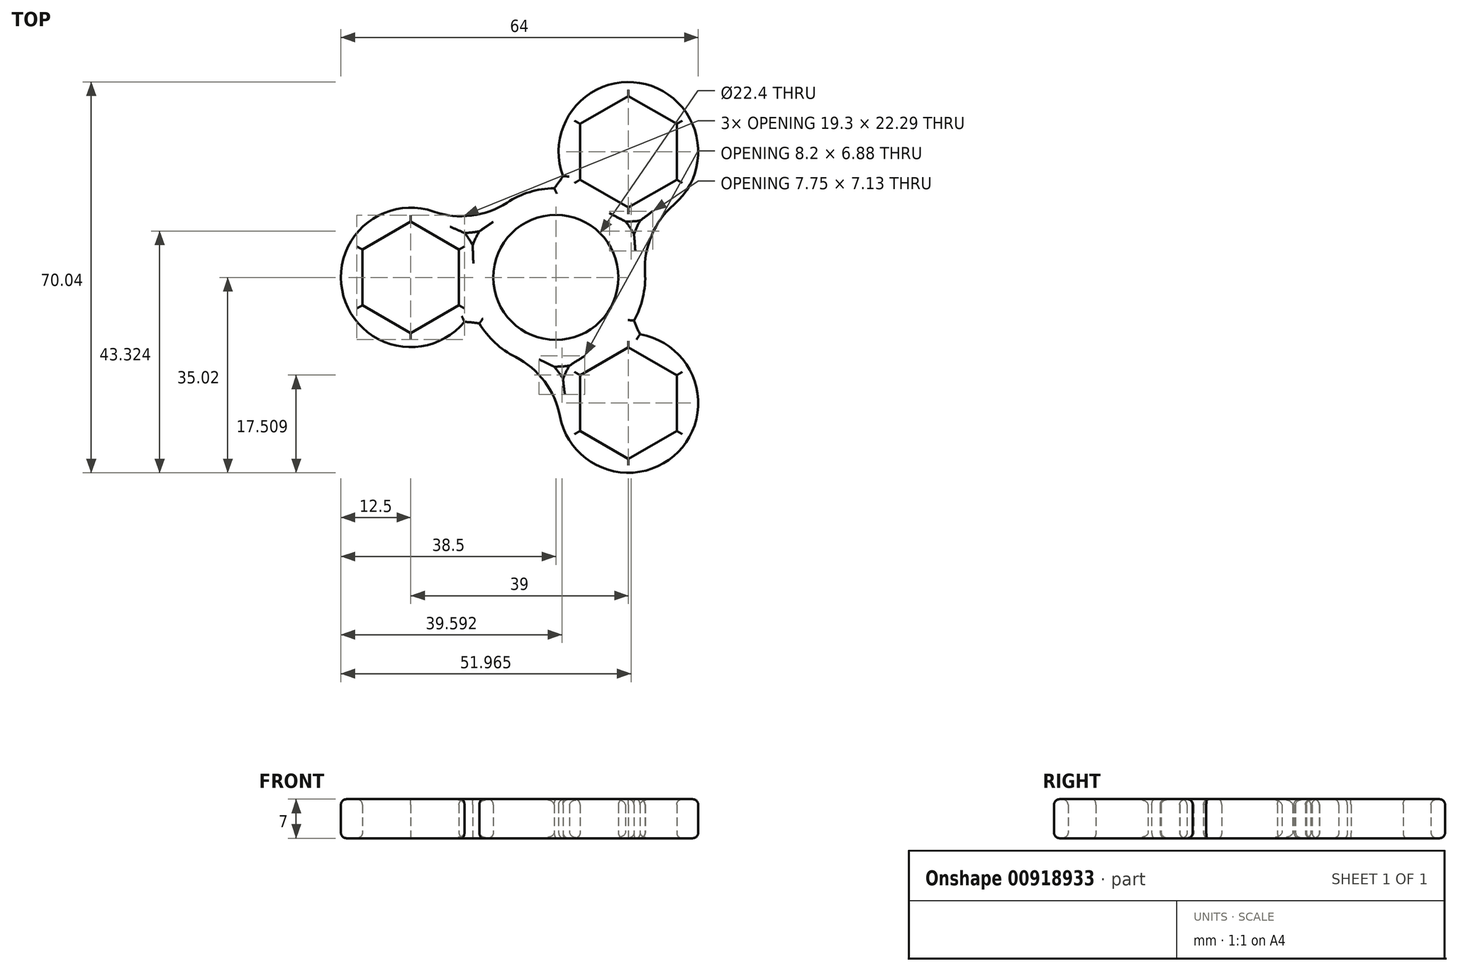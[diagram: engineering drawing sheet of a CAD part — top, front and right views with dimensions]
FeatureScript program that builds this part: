
annotation { "Feature Type Name" : "Feature", "Feature Type Description" : "" }
export const myFeature = defineFeature(function(context is Context, id is Id, definition is map)
    precondition{}
    {
        {
            var Q0;
            Q0=qCreatedBy(makeId("Top.planeOp"),FACE);
            var sketch = newSketch(context, id + "F0", { "sketchPlane" : qUnion([Q0])});
            skCircle(sketch, "E0", {"center": v(0, 0) * mm, "radius": 11.2 * mm});
            skCircle(sketch, "E1", {"center": v(0, 0) * mm, "radius": 16 * mm});
            skLineSegment(sketch, "E2", {"start": v(0, 0) * mm, "end": v(-26, 0) * mm, "construction": true});
            skCircle(sketch, "E3", {"center": v(-26, 0) * mm, "radius": 12.5 * mm});
            skArc(sketch, "E4", {"start": v(-21.88, 11.8) * mm, "mid": v(-15.13, 11.07) * mm, "end": v(-8.74, 13.4) * mm});
            skArc(sketch, "E5", {"start": v(-16.37, 7.97) * mm, "mid": v(-15.03, 8.06) * mm, "end": v(-13.7, 8.26) * mm});
            skArc(sketch, "E6.MirrorCS", {"start": v(-16.37, -7.97) * mm, "mid": v(-15.03, -8.06) * mm, "end": v(-13.7, -8.26) * mm});
            skArc(sketch, "E7.MirrorCS", {"start": v(-21.88, -11.8) * mm, "mid": v(-15.13, -11.07) * mm, "end": v(-8.74, -13.4) * mm});
            skLineSegment(sketch, "E8.1.0", {"start": v(0, 0) * mm, "end": v(13, -22.52) * mm, "construction": true});
            skCircle(sketch, "E8.1.1", {"center": v(13, -22.52) * mm, "radius": 12.5 * mm});
            skArc(sketch, "E8.1.2", {"start": v(0.72, -24.85) * mm, "mid": v(-2.03, -18.64) * mm, "end": v(-7.23, -14.27) * mm});
            skArc(sketch, "E8.1.3", {"start": v(1.28, -18.17) * mm, "mid": v(0.53, -17.05) * mm, "end": v(-0.3, -16) * mm});
            skArc(sketch, "E8.1.4", {"start": v(15.1, -10.2) * mm, "mid": v(14.5, -8.99) * mm, "end": v(14, -7.74) * mm});
            skArc(sketch, "E8.1.5", {"start": v(21.16, -13.05) * mm, "mid": v(17.15, -7.56) * mm, "end": v(15.98, -0.87) * mm});
            skLineSegment(sketch, "E8.2.0", {"start": v(0, 0) * mm, "end": v(13, 22.52) * mm, "construction": true});
            skCircle(sketch, "E8.2.1", {"center": v(13, 22.52) * mm, "radius": 12.5 * mm});
            skArc(sketch, "E8.2.2", {"start": v(21.16, 13.05) * mm, "mid": v(17.15, 7.56) * mm, "end": v(15.98, 0.87) * mm});
            skArc(sketch, "E8.2.3", {"start": v(15.1, 10.2) * mm, "mid": v(14.5, 8.99) * mm, "end": v(14, 7.74) * mm});
            skArc(sketch, "E8.2.4", {"start": v(1.28, 18.17) * mm, "mid": v(0.53, 17.05) * mm, "end": v(-0.3, 16) * mm});
            skArc(sketch, "E8.2.5", {"start": v(0.72, 24.85) * mm, "mid": v(-2.03, 18.64) * mm, "end": v(-7.23, 14.27) * mm});
            skCircle(sketch, "E9.cCircle", {"center": v(-26, 0) * mm, "radius": 8.65 * mm, "construction": true});
            skLineSegment(sketch, "E9.0", {"start": v(-17.35, 5) * mm, "end": v(-17.35, -5) * mm});
            skLineSegment(sketch, "E9.1", {"start": v(-17.35, -5) * mm, "end": v(-26, -9.99) * mm});
            skLineSegment(sketch, "E9.2", {"start": v(-26, -9.99) * mm, "end": v(-34.65, -5) * mm});
            skLineSegment(sketch, "E9.3", {"start": v(-34.65, -5) * mm, "end": v(-34.65, 5) * mm});
            skLineSegment(sketch, "E9.4", {"start": v(-34.65, 5) * mm, "end": v(-26, 9.99) * mm});
            skLineSegment(sketch, "E9.5", {"start": v(-26, 9.99) * mm, "end": v(-17.35, 5) * mm});
            skPoint(sketch, "E9.0.midPoint", {"position": v(-17.35, 0) * mm});
            skLineSegment(sketch, "E10.1.1", {"start": v(13, -32.5) * mm, "end": v(4.35, -27.51) * mm});
            skLineSegment(sketch, "E10.1.2", {"start": v(4.35, -27.51) * mm, "end": v(4.35, -17.52) * mm});
            skLineSegment(sketch, "E10.1.3", {"start": v(4.35, -17.52) * mm, "end": v(13, -12.53) * mm});
            skLineSegment(sketch, "E10.1.4", {"start": v(13, -12.53) * mm, "end": v(21.65, -17.52) * mm});
            skLineSegment(sketch, "E10.1.5", {"start": v(21.65, -17.52) * mm, "end": v(21.65, -27.51) * mm});
            skLineSegment(sketch, "E10.1.6", {"start": v(21.65, -27.51) * mm, "end": v(13, -32.5) * mm});
            skLineSegment(sketch, "E10.2.1", {"start": v(21.65, 27.51) * mm, "end": v(21.65, 17.52) * mm});
            skLineSegment(sketch, "E10.2.2", {"start": v(21.65, 17.52) * mm, "end": v(13, 12.53) * mm});
            skLineSegment(sketch, "E10.2.3", {"start": v(13, 12.53) * mm, "end": v(4.35, 17.52) * mm});
            skLineSegment(sketch, "E10.2.4", {"start": v(4.35, 17.52) * mm, "end": v(4.35, 27.51) * mm});
            skLineSegment(sketch, "E10.2.5", {"start": v(4.35, 27.51) * mm, "end": v(13, 32.5) * mm});
            skLineSegment(sketch, "E10.2.6", {"start": v(13, 32.5) * mm, "end": v(21.65, 27.51) * mm});
            skSolve(sketch);
        }
        {
            var Q0;
            {var subQ0=sQuery(id+"F0.wireOp",EDGE,"E3");var subQ4=sQuery(id+"F0.wireOp",EDGE,"E1");var subQ5=makeQuery(id+"F0.imprint","INTERSECT",VERTEX,{"disambiguationData":[OD(0.0)],"derivedFrom":[subQ4,subQ0]});Q0=makeQuery(id+"F0.imprint","IMPRINT",FACE,{"disambiguationData":[TD([[makeQuery(id+"F0.imprint","IMPRINT",EDGE,{"disambiguationData":[TD([[subQ5,-1.0]])],"derivedFrom":subQ4}),-1.0]])]});}
            var Q1;
            {var subQ0=sQuery(id+"F0.wireOp",EDGE,"E3");var subQ1=sQuery(id+"F0.wireOp",EDGE,"E1");var subQ2=makeQuery(id+"F0.imprint","INTERSECT",VERTEX,{"disambiguationData":[OD(0.0)],"derivedFrom":[subQ1,subQ0]});Q1=makeQuery(id+"F0.imprint","IMPRINT",FACE,{"disambiguationData":[TD([[makeQuery(id+"F0.imprint","IMPRINT",EDGE,{"disambiguationData":[TD([[subQ2,-1.0]])],"derivedFrom":subQ1}),1.0]])]});}
            var Q2;
            Q2=makeQuery(id+"F0.imprint","IMPRINT",FACE,{"disambiguationData":[TD([[makeQuery(id+"F0.imprint","IMPRINT",EDGE,{"derivedFrom":sQuery(id+"F0.wireOp",EDGE,"E0")}),-1.0]])]});
            var Q3;
            {var subQ0=sQuery(id+"F0.wireOp",EDGE,"E4");Q3=makeQuery(id+"F0.imprint","IMPRINT",FACE,{"disambiguationData":[TD([[makeQuery(id+"F0.imprint","IMPRINT",EDGE,{"derivedFrom":subQ0}),-1.0]])]});}
            var Q4;
            {var subQ0=sQuery(id+"F0.wireOp",EDGE,"E8.2.4");Q4=makeQuery(id+"F0.imprint","IMPRINT",FACE,{"disambiguationData":[TD([[makeQuery(id+"F0.imprint","IMPRINT",EDGE,{"derivedFrom":subQ0}),-1.0]])]});}
            var Q5;
            {var subQ0=sQuery(id+"F0.wireOp",EDGE,"E8.2.1");var subQ4=sQuery(id+"F0.wireOp",EDGE,"E1");var subQ5=makeQuery(id+"F0.imprint","INTERSECT",VERTEX,{"disambiguationData":[OD(0.0)],"derivedFrom":[subQ4,subQ0]});Q5=makeQuery(id+"F0.imprint","IMPRINT",FACE,{"disambiguationData":[TD([[makeQuery(id+"F0.imprint","IMPRINT",EDGE,{"disambiguationData":[TD([[subQ5,-1.0]])],"derivedFrom":subQ4}),-1.0]])]});}
            var Q6;
            {var subQ0=sQuery(id+"F0.wireOp",EDGE,"E8.2.1");var subQ1=sQuery(id+"F0.wireOp",EDGE,"E1");var subQ2=makeQuery(id+"F0.imprint","INTERSECT",VERTEX,{"disambiguationData":[OD(0.0)],"derivedFrom":[subQ1,subQ0]});Q6=makeQuery(id+"F0.imprint","IMPRINT",FACE,{"disambiguationData":[TD([[makeQuery(id+"F0.imprint","IMPRINT",EDGE,{"disambiguationData":[TD([[subQ2,-1.0]])],"derivedFrom":subQ1}),1.0]])]});}
            var Q7;
            {var subQ0=sQuery(id+"F0.wireOp",EDGE,"E8.2.2");Q7=makeQuery(id+"F0.imprint","IMPRINT",FACE,{"disambiguationData":[TD([[makeQuery(id+"F0.imprint","IMPRINT",EDGE,{"derivedFrom":subQ0}),-1.0]])]});}
            var Q8;
            {var subQ0=sQuery(id+"F0.wireOp",EDGE,"E8.1.4");Q8=makeQuery(id+"F0.imprint","IMPRINT",FACE,{"disambiguationData":[TD([[makeQuery(id+"F0.imprint","IMPRINT",EDGE,{"derivedFrom":subQ0}),-1.0]])]});}
            var Q9;
            {var subQ0=sQuery(id+"F0.wireOp",EDGE,"E8.1.1");var subQ4=sQuery(id+"F0.wireOp",EDGE,"E1");var subQ5=makeQuery(id+"F0.imprint","INTERSECT",VERTEX,{"disambiguationData":[OD(0.0)],"derivedFrom":[subQ4,subQ0]});Q9=makeQuery(id+"F0.imprint","IMPRINT",FACE,{"disambiguationData":[TD([[makeQuery(id+"F0.imprint","IMPRINT",EDGE,{"disambiguationData":[TD([[subQ5,-1.0]])],"derivedFrom":subQ4}),-1.0]])]});}
            var Q10;
            {var subQ0=sQuery(id+"F0.wireOp",EDGE,"E8.1.1");var subQ1=sQuery(id+"F0.wireOp",EDGE,"E1");var subQ2=makeQuery(id+"F0.imprint","INTERSECT",VERTEX,{"disambiguationData":[OD(0.0)],"derivedFrom":[subQ1,subQ0]});Q10=makeQuery(id+"F0.imprint","IMPRINT",FACE,{"disambiguationData":[TD([[makeQuery(id+"F0.imprint","IMPRINT",EDGE,{"disambiguationData":[TD([[subQ2,-1.0]])],"derivedFrom":subQ1}),1.0]])]});}
            var Q11;
            {var subQ0=sQuery(id+"F0.wireOp",EDGE,"E8.1.2");Q11=makeQuery(id+"F0.imprint","IMPRINT",FACE,{"disambiguationData":[TD([[makeQuery(id+"F0.imprint","IMPRINT",EDGE,{"derivedFrom":subQ0}),-1.0]])]});}
            var Q12;
            {var subQ0=sQuery(id+"F0.wireOp",EDGE,"E6.MirrorCS");Q12=makeQuery(id+"F0.imprint","IMPRINT",FACE,{"disambiguationData":[TD([[makeQuery(id+"F0.imprint","IMPRINT",EDGE,{"derivedFrom":subQ0}),-1.0]])]});}
            extrude(context, id + "F1", {"entities" : qUnion([Q0, Q1, Q2, Q3, Q4, Q5, Q6, Q7, Q8, Q9, Q10, Q11, Q12]), "depth" : 7 * mm, "offsetDistance" : 25 * mm});
        }
        {
            var Q0;
            Q0=makeQuery(id+"F1.opExtrude","CAP_FACE",FACE,{"disambiguationData":[OSD([sQuery(id+"F0.wireOp",EDGE,"E0"),sQuery(id+"F0.wireOp",EDGE,"E1"),sQuery(id+"F0.wireOp",EDGE,"E3"),sQuery(id+"F0.wireOp",EDGE,"E4"),sQuery(id+"F0.wireOp",EDGE,"E5"),sQuery(id+"F0.wireOp",EDGE,"E6.MirrorCS"),sQuery(id+"F0.wireOp",EDGE,"E7.MirrorCS"),sQuery(id+"F0.wireOp",EDGE,"E8.1.1"),sQuery(id+"F0.wireOp",EDGE,"E8.1.2"),sQuery(id+"F0.wireOp",EDGE,"E8.1.3"),sQuery(id+"F0.wireOp",EDGE,"E8.1.4"),sQuery(id+"F0.wireOp",EDGE,"E8.1.5"),sQuery(id+"F0.wireOp",EDGE,"E8.2.1"),sQuery(id+"F0.wireOp",EDGE,"E8.2.2"),sQuery(id+"F0.wireOp",EDGE,"E8.2.3"),sQuery(id+"F0.wireOp",EDGE,"E8.2.4"),sQuery(id+"F0.wireOp",EDGE,"E8.2.5")])],"isStart":false});
            var Q1;
            Q1=makeQuery(id+"F1.opExtrude","CAP_FACE",FACE,{"disambiguationData":[OSD([sQuery(id+"F0.wireOp",EDGE,"E0"),sQuery(id+"F0.wireOp",EDGE,"E1"),sQuery(id+"F0.wireOp",EDGE,"E3"),sQuery(id+"F0.wireOp",EDGE,"E4"),sQuery(id+"F0.wireOp",EDGE,"E5"),sQuery(id+"F0.wireOp",EDGE,"E6.MirrorCS"),sQuery(id+"F0.wireOp",EDGE,"E7.MirrorCS"),sQuery(id+"F0.wireOp",EDGE,"E8.1.1"),sQuery(id+"F0.wireOp",EDGE,"E8.1.2"),sQuery(id+"F0.wireOp",EDGE,"E8.1.3"),sQuery(id+"F0.wireOp",EDGE,"E8.1.4"),sQuery(id+"F0.wireOp",EDGE,"E8.1.5"),sQuery(id+"F0.wireOp",EDGE,"E8.2.1"),sQuery(id+"F0.wireOp",EDGE,"E8.2.2"),sQuery(id+"F0.wireOp",EDGE,"E8.2.3"),sQuery(id+"F0.wireOp",EDGE,"E8.2.4"),sQuery(id+"F0.wireOp",EDGE,"E8.2.5")])],"isStart":true});
            fillet(context, id + "F2", {"entities" : qUnion([Q0, Q1]), "radius" : 1 * mm, "tangentPropagation" : true, "allowEdgeOverflow" : false});
        }
    });
